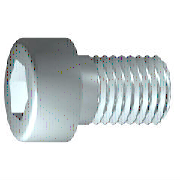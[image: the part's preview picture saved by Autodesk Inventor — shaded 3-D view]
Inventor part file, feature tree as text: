
AUTODESK INVENTOR PART (.ipt)
format: ipt  version: 2022 (Build 260153000, 153)  size: 189,952 bytes
history: native  units: mm (DEFAULTED — no unit token found)
features: sketch x2, extrude x1, plane x1
ambient origin geometry x7: Origin, YZ Plane, XY Plane, X Axis, Y Axis, Z Axis, Center Point
bodies: Solid1 (feature_tree), Body (feature_tree)
feature tree (4):
  extrude  "Slot"  Depth=0.61345mm
  plane  "Work Plane1"
  sketch  "Sketch1"  dims[d0=23.1731mm d1=0.61345mm]
  sketch  "Sketch2"  dims[d2=6.0mm d3=3.0mm d4=60.0deg d5=6.0mm d6=6.0mm d7=5.773503mm d8=10.0mm d10=90.0deg d11=10.0mm d9=0.0mm d12=23.1731mm d13=0.0mm d14=0.61345mm d15=0.61345mm d16=0.6mm d17=0.0mm d18=0.0mm d19=25.0mm d27=45.0deg d28=0.25mm d29=0.25mm]
